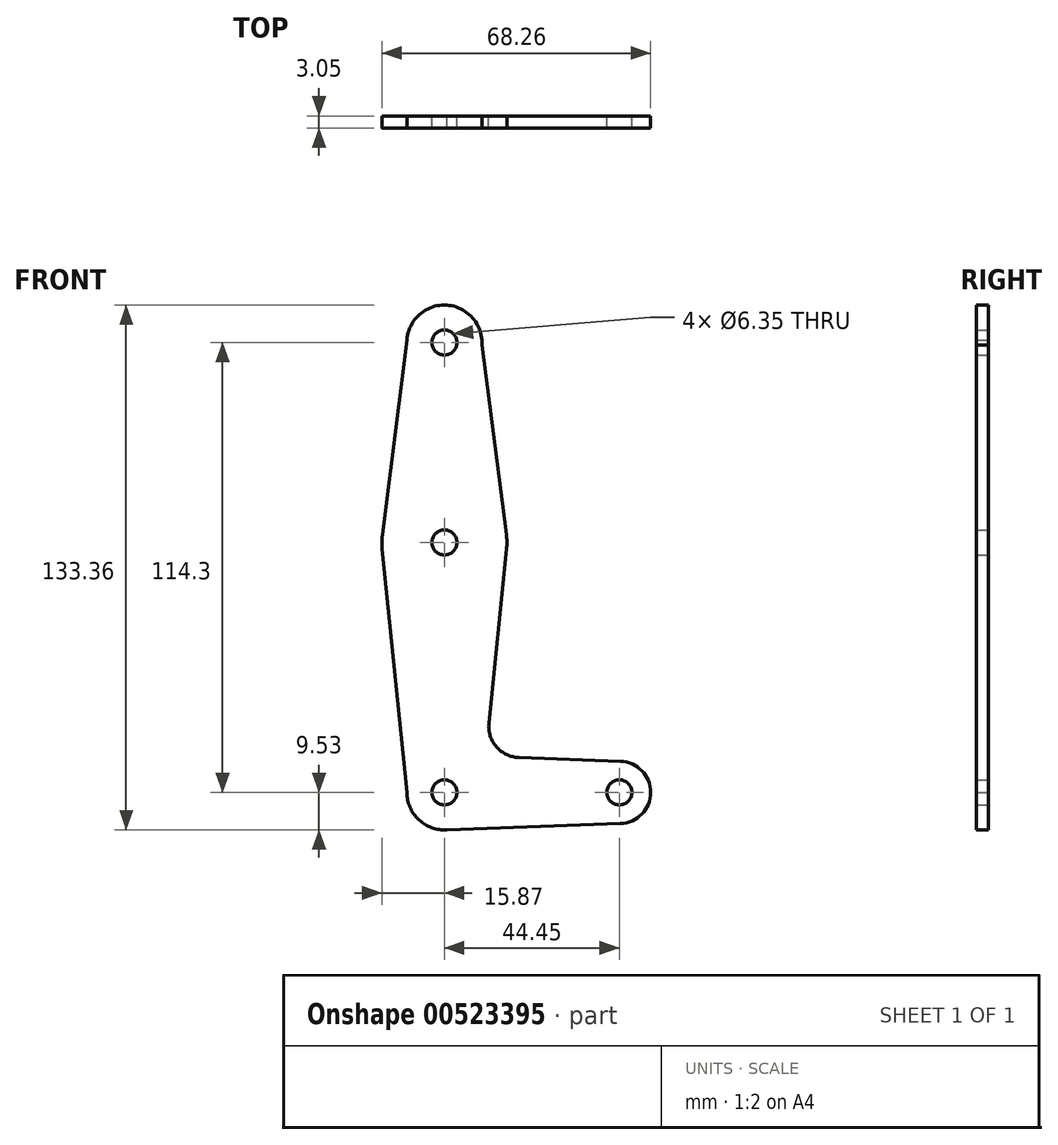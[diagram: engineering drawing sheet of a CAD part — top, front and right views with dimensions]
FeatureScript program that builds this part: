
annotation { "Feature Type Name" : "Feature", "Feature Type Description" : "" }
export const myFeature = defineFeature(function(context is Context, id is Id, definition is map)
    precondition{}
    {
        {
            var Q0;
            Q0=qCreatedBy(makeId("Front.planeOp"),FACE);
            var sketch = newSketch(context, id + "F0", { "sketchPlane" : qUnion([Q0])});
            skLineSegment(sketch, "E0", {"start": v(0, 0) * mm, "end": v(44.45, 0) * mm, "construction": true});
            skCircle(sketch, "E1", {"center": v(0, 114.3) * mm, "radius": 9.53 * mm});
            skCircle(sketch, "E2", {"center": v(0, 63.5) * mm, "radius": 15.88 * mm});
            skCircle(sketch, "E3", {"center": v(0, 0) * mm, "radius": 9.53 * mm});
            skCircle(sketch, "E4", {"center": v(44.45, 0) * mm, "radius": 7.94 * mm});
            skLineSegment(sketch, "E5", {"start": v(0, 63.5) * mm, "end": v(0, 0) * mm, "construction": true});
            skLineSegment(sketch, "E6", {"start": v(0, 63.5) * mm, "end": v(0, 114.3) * mm, "construction": true});
            skLineSegment(sketch, "E7", {"start": v(-9.5, 114.92) * mm, "end": v(-15.75, 65.49) * mm});
            skLineSegment(sketch, "E8", {"start": v(9.5, 113.67) * mm, "end": v(15.74, 65.54) * mm});
            skLineSegment(sketch, "E9", {"start": v(-9.52, 0) * mm, "end": v(-15.8, 61.9) * mm});
            skLineSegment(sketch, "E10", {"start": v(11.3, 17.6) * mm, "end": v(15.8, 61.9) * mm});
            skCircle(sketch, "E11", {"center": v(0, 114.3) * mm, "radius": 3.18 * mm});
            skCircle(sketch, "E12", {"center": v(0, 63.5) * mm, "radius": 3.18 * mm});
            skCircle(sketch, "E13", {"center": v(0, 0) * mm, "radius": 3.18 * mm});
            skCircle(sketch, "E14", {"center": v(44.45, 0) * mm, "radius": 3.18 * mm});
            skLineSegment(sketch, "E15", {"start": v(18.93, 8.85) * mm, "end": v(44.73, 7.93) * mm});
            skLineSegment(sketch, "E16", {"start": v(0, -9.53) * mm, "end": v(44.73, -7.93) * mm});
            skArc(sketch, "E17.filletArc", {"start": v(11.3, 17.6) * mm, "mid": v(13.22, 11.57) * mm, "end": v(18.93, 8.85) * mm});
            skSolve(sketch);
        }
        {
            var Q0;
            Q0 = qSketchRegion(id + "F0", true);
            extrude(context, id + "F1", {"entities" : qUnion([Q0]), "depth" : 3.05 * mm, "offsetDistance" : 25.4 * mm});
        }
    });
